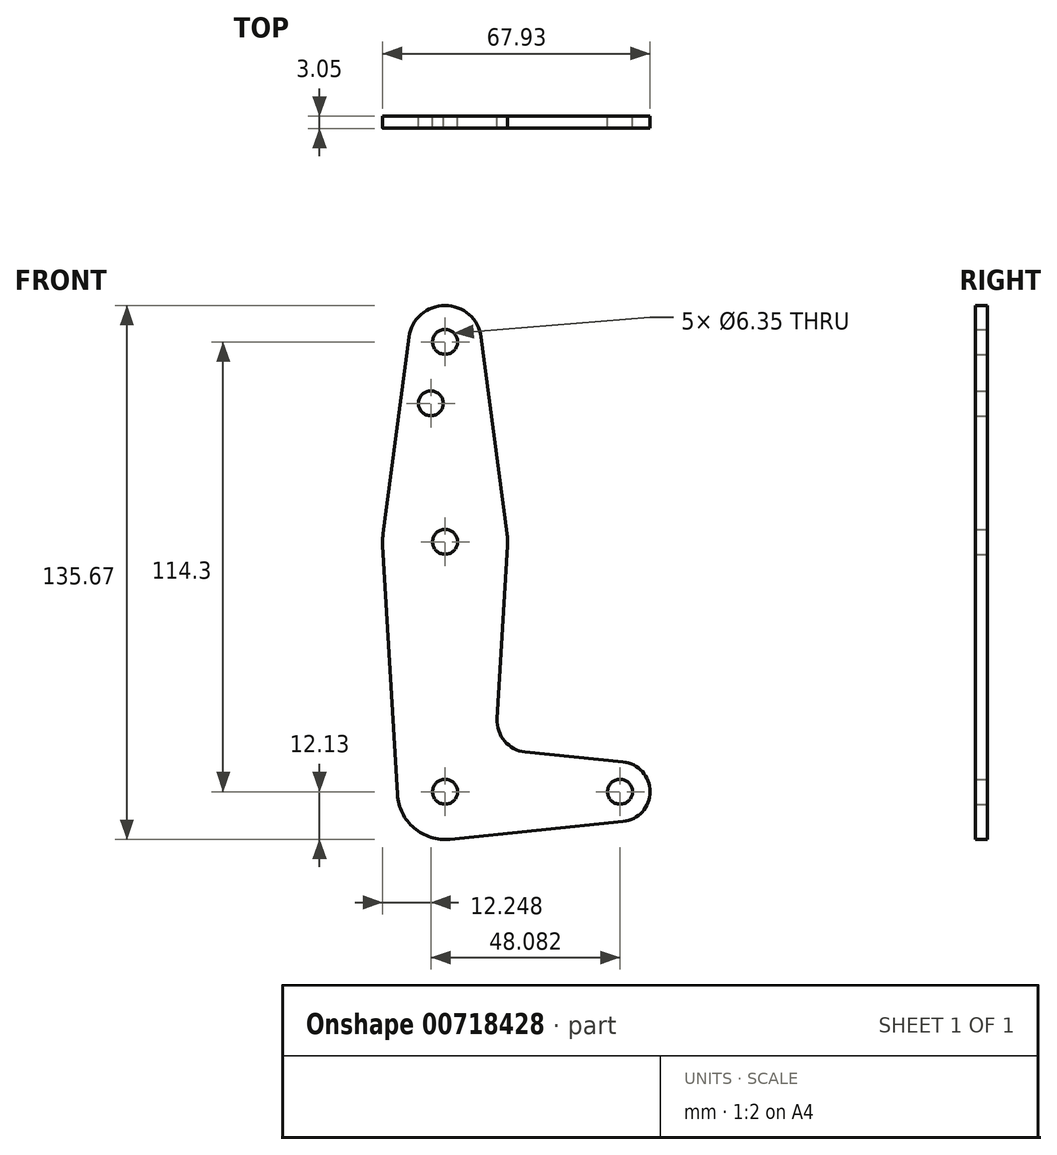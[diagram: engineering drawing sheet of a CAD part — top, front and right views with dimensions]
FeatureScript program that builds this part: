
annotation { "Feature Type Name" : "Feature", "Feature Type Description" : "" }
export const myFeature = defineFeature(function(context is Context, id is Id, definition is map)
    precondition{}
    {
        {
            var Q0;
            Q0=qCreatedBy(makeId("Front.planeOp"),FACE);
            var sketch = newSketch(context, id + "F0", { "sketchPlane" : qUnion([Q0])});
            skLineSegment(sketch, "E0", {"start": v(0, 0) * mm, "end": v(44.45, 0) * mm});
            skLineSegment(sketch, "E1", {"start": v(0, 0) * mm, "end": v(0, 114.3) * mm});
            skCircle(sketch, "E2", {"center": v(0, 114.3) * mm, "radius": 9.24 * mm});
            skCircle(sketch, "E3", {"center": v(0, 0) * mm, "radius": 12.13 * mm});
            skCircle(sketch, "E4", {"center": v(44.45, 0) * mm, "radius": 7.6 * mm});
            skCircle(sketch, "E5", {"center": v(0, 63.5) * mm, "radius": 15.88 * mm});
            skLineSegment(sketch, "E6", {"start": v(-9.16, 115.5) * mm, "end": v(-15.74, 65.57) * mm});
            skLineSegment(sketch, "E7", {"start": v(9.16, 115.5) * mm, "end": v(15.74, 65.57) * mm});
            skLineSegment(sketch, "E8", {"start": v(15.85, 62.56) * mm, "end": v(13.24, 18.49) * mm});
            skLineSegment(sketch, "E9", {"start": v(20.37, 10.1) * mm, "end": v(45.22, 7.56) * mm});
            skCircle(sketch, "E10", {"center": v(0, 114.3) * mm, "radius": 3.18 * mm});
            skCircle(sketch, "E11", {"center": v(0, 63.5) * mm, "radius": 3.18 * mm});
            skCircle(sketch, "E12", {"center": v(0, 0) * mm, "radius": 3.17 * mm});
            skCircle(sketch, "E13", {"center": v(44.45, 0) * mm, "radius": 3.18 * mm});
            skCircle(sketch, "E14", {"center": v(-3.63, 98.68) * mm, "radius": 3.18 * mm});
            skArc(sketch, "E15.filletArc", {"start": v(13.24, 18.49) * mm, "mid": v(15.12, 12.86) * mm, "end": v(20.37, 10.1) * mm});
            skPoint(sketch, "E16.end.orphan", {"position": v(-12.15, 0) * mm});
            skLineSegment(sketch, "E17", {"start": v(-15.85, 62.56) * mm, "end": v(-12.1, -0.72) * mm});
            skLineSegment(sketch, "E18", {"start": v(1.23, -12.07) * mm, "end": v(45.22, -7.56) * mm});
            skSolve(sketch);
        }
        {
            var Q0;
            Q0 = qSketchRegion(id + "F0", true);
            var Q1;
            {var subQ0=sQuery(id+"F0.wireOp",EDGE,"E12");var subQ1=sQuery(id+"F0.wireOp",EDGE,"E0");var subQ2=makeQuery(id+"F0.imprint","INTERSECT",VERTEX,{"derivedFrom":[subQ1,subQ0]});Q1=makeQuery(id+"F0.imprint","IMPRINT",FACE,{"disambiguationData":[TD([[makeQuery(id+"F0.imprint","IMPRINT",EDGE,{"disambiguationData":[TD([[subQ2,-1.0]])],"derivedFrom":subQ1}),1.0]])]});}
            extrude(context, id + "F1", {"entities" : qUnion([Q0, Q1]), "depth" : 3.05 * mm, "offsetDistance" : 25.4 * mm});
        }
    });
